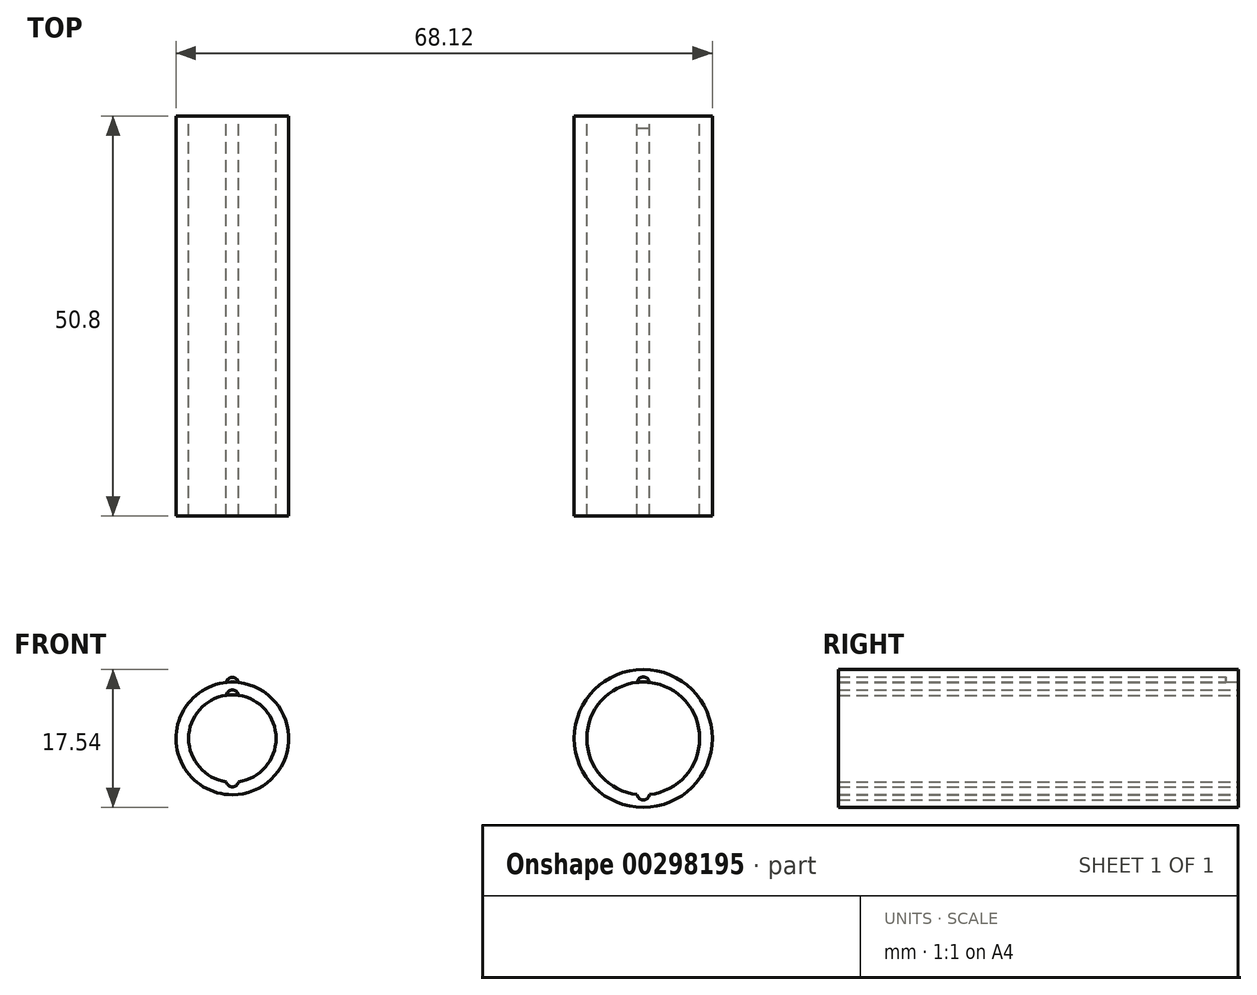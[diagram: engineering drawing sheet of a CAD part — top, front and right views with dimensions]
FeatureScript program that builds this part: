
annotation { "Feature Type Name" : "Feature", "Feature Type Description" : "" }
export const myFeature = defineFeature(function(context is Context, id is Id, definition is map)
    precondition{}
    {
        {
            var Q0;
            Q0=qCreatedBy(makeId("Front.planeOp"),FACE);
            var sketch = newSketch(context, id + "F0", { "sketchPlane" : qUnion([Q0])});
            skCircle(sketch, "E0", {"center": v(-52.2, 0) * mm, "radius": 5.55 * mm});
            skArc(sketch, "E1", {"start": v(-51.41, 5.5) * mm, "mid": v(-52.2, 6.15) * mm, "end": v(-52.98, 5.5) * mm});
            skArc(sketch, "E2.MirrorCS", {"start": v(-51.41, -5.5) * mm, "mid": v(-52.2, -6.15) * mm, "end": v(-52.98, -5.5) * mm});
            skCircle(sketch, "E3", {"center": v(-52.2, 0) * mm, "radius": 7.16 * mm});
            skArc(sketch, "E4", {"start": v(-51.41, 7.11) * mm, "mid": v(-52.2, 7.75) * mm, "end": v(-52.98, 7.11) * mm});
            skArc(sketch, "E5.MirrorCS", {"start": v(-51.41, -7.11) * mm, "mid": v(-52.2, -7.75) * mm, "end": v(-52.98, -7.11) * mm});
            skSolve(sketch);
        }
        {
            var Q0;
            {var subQ0=sQuery(id+"F0.wireOp",EDGE,"989fonS6-DCI9-Xsph-8poP-fN17gT7lNFCT");var subQ3=sQuery(id+"F0.wireOp",EDGE,"9SPTYYTQ-VdL9-9Wax-ncZg-mlvlZ5eD6Vp3");var subQ5=makeQuery(id+"F0.imprint","INTERSECT",VERTEX,{"derivedFrom":[subQ0,subQ3]});Q0=makeQuery(id+"F0.imprint","IMPRINT",FACE,{"disambiguationData":[TD([[makeQuery(id+"F0.imprint","IMPRINT",EDGE,{"disambiguationData":[TD([[subQ5,-1.0]])],"derivedFrom":subQ0}),1.0]])]});}
            var Q1;
            {var subQ1=sQuery(id+"F0.wireOp",EDGE,"989fonS6-DCI9-Xsph-8poP-fN17gT7lNFCT");var subQ4=sQuery(id+"F0.wireOp",EDGE,"9SPTYYTQ-VdL9-9Wax-ncZg-mlvlZ5eD6Vp3");var subQ6=makeQuery(id+"F0.imprint","INTERSECT",VERTEX,{"derivedFrom":[subQ1,subQ4]});Q1=makeQuery(id+"F0.imprint","IMPRINT",FACE,{"disambiguationData":[TD([[makeQuery(id+"F0.imprint","IMPRINT",EDGE,{"disambiguationData":[TD([[subQ6,-1.0]])],"derivedFrom":subQ1}),-1.0]])]});}
            var Q2;
            {var subQ0=sQuery(id+"F0.wireOp",EDGE,"umcB0eHT-4so1-jZ8v-9NKV-PrQTAY5CJR8B");Q2=makeQuery(id+"F0.imprint","IMPRINT",FACE,{"disambiguationData":[TD([[makeQuery(id+"F0.imprint","IMPRINT",EDGE,{"derivedFrom":subQ0}),-1.0]])]});}
            var Q3;
            {var subQ0=sQuery(id+"F0.wireOp",EDGE,"f3edb4b3-b429-4efd-8aee-323062dacc900.MirrorCS");var subQ1=sQuery(id+"F0.wireOp",EDGE,"izCre8lw-zIuZ-BvPA-PBmO-Y99l2bE8kLr2");var subQ2=makeQuery(id+"F0.imprint","INTERSECT",VERTEX,{"disambiguationData":[OD(1.0)],"derivedFrom":[subQ1,subQ0]});Q3=makeQuery(id+"F0.imprint","IMPRINT",FACE,{"disambiguationData":[TD([[makeQuery(id+"F0.imprint","IMPRINT",EDGE,{"disambiguationData":[TD([[subQ2,-1.0]])],"derivedFrom":subQ1}),-1.0]])]});}
            var Q4;
            {var subQ0=sQuery(id+"F0.wireOp",EDGE,"f3edb4b3-b429-4efd-8aee-323062dacc900.MirrorCS");var subQ1=sQuery(id+"F0.wireOp",EDGE,"izCre8lw-zIuZ-BvPA-PBmO-Y99l2bE8kLr2");var subQ2=makeQuery(id+"F0.imprint","INTERSECT",VERTEX,{"disambiguationData":[OD(0.0)],"derivedFrom":[subQ1,subQ0]});Q4=makeQuery(id+"F0.imprint","IMPRINT",FACE,{"disambiguationData":[TD([[makeQuery(id+"F0.imprint","IMPRINT",EDGE,{"disambiguationData":[TD([[subQ2,1.0]])],"derivedFrom":subQ1}),-1.0]])]});}
            var Q5;
            {var subQ0=sQuery(id+"F0.wireOp",EDGE,"989fonS6-DCI9-Xsph-8poP-fN17gT7lNFCT");var subQ5=sQuery(id+"F0.wireOp",EDGE,"E1");var subQ6=makeQuery(id+"F0.imprint","INTERSECT",VERTEX,{"derivedFrom":[subQ0,subQ5]});Q5=makeQuery(id+"F0.imprint","IMPRINT",FACE,{"disambiguationData":[TD([[makeQuery(id+"F0.imprint","IMPRINT",EDGE,{"disambiguationData":[TD([[subQ6,1.0]])],"derivedFrom":subQ0}),1.0]])]});}
            var Q6;
            {var subQ0=sQuery(id+"F0.wireOp",EDGE,"umcB0eHT-4so1-jZ8v-9NKV-PrQTAY5CJR8B");Q6=makeQuery(id+"F0.imprint","IMPRINT",FACE,{"disambiguationData":[TD([[makeQuery(id+"F0.imprint","IMPRINT",EDGE,{"derivedFrom":subQ0}),1.0]])]});}
            var Q7;
            {var subQ1=sQuery(id+"F0.wireOp",EDGE,"izCre8lw-zIuZ-BvPA-PBmO-Y99l2bE8kLr2");var subQ9=makeQuery(id+"F0.imprint","INTERSECT",VERTEX,{"disambiguationData":[OD(1.0)],"derivedFrom":[subQ1,sQuery(id+"F0.wireOp",EDGE,"f3edb4b3-b429-4efd-8aee-323062dacc900.MirrorCS")]});Q7=makeQuery(id+"F0.imprint","IMPRINT",FACE,{"disambiguationData":[TD([[makeQuery(id+"F0.imprint","IMPRINT",EDGE,{"disambiguationData":[TD([[subQ9,-1.0]])],"derivedFrom":subQ1}),1.0]])]});}
            var Q8;
            {var subQ1=sQuery(id+"F0.wireOp",EDGE,"izCre8lw-zIuZ-BvPA-PBmO-Y99l2bE8kLr2");var subQ10=makeQuery(id+"F0.imprint","INTERSECT",VERTEX,{"disambiguationData":[OD(0.0)],"derivedFrom":[subQ1,sQuery(id+"F0.wireOp",EDGE,"f3edb4b3-b429-4efd-8aee-323062dacc900.MirrorCS")]});Q8=makeQuery(id+"F0.imprint","IMPRINT",FACE,{"disambiguationData":[TD([[makeQuery(id+"F0.imprint","IMPRINT",EDGE,{"disambiguationData":[TD([[subQ10,1.0]])],"derivedFrom":subQ1}),1.0]])]});}
            var Q9;
            {var subQ1=sQuery(id+"F0.wireOp",EDGE,"E1");Q9=makeQuery(id+"F0.imprint","IMPRINT",FACE,{"disambiguationData":[TD([[makeQuery(id+"F0.imprint","IMPRINT",EDGE,{"derivedFrom":subQ1}),-1.0]])]});}
            extrude(context, id + "F1", {"entities" : qUnion([Q0, Q1, Q2, Q3, Q4, Q5, Q6, Q7, Q8, Q9]), "depth" : 50.8 * mm});
        }
        {
            var Q0;
            {var subQ0=sQuery(id+"F0.wireOp",EDGE,"E4");var subQ1=sQuery(id+"F0.wireOp",EDGE,"989fonS6-DCI9-Xsph-8poP-fN17gT7lNFCT");var subQ2=makeQuery(id+"F0.imprint","INTERSECT",VERTEX,{"derivedFrom":[subQ1,subQ0]});Q0=makeQuery(id+"F0.imprint","IMPRINT",FACE,{"disambiguationData":[TD([[makeQuery(id+"F0.imprint","IMPRINT",EDGE,{"disambiguationData":[TD([[subQ2,-1.0]])],"derivedFrom":subQ1}),-1.0]])]});}
            var Q1;
            {var subQ0=sQuery(id+"F0.wireOp",EDGE,"E4");var subQ1=sQuery(id+"F0.wireOp",EDGE,"989fonS6-DCI9-Xsph-8poP-fN17gT7lNFCT");var subQ2=makeQuery(id+"F0.imprint","INTERSECT",VERTEX,{"derivedFrom":[subQ1,subQ0]});Q1=makeQuery(id+"F0.imprint","IMPRINT",FACE,{"disambiguationData":[TD([[makeQuery(id+"F0.imprint","IMPRINT",EDGE,{"disambiguationData":[TD([[subQ2,-1.0]])],"derivedFrom":subQ1}),1.0]])]});}
            var Q2;
            {var subQ0=sQuery(id+"F0.wireOp",EDGE,"E1");var subQ1=sQuery(id+"F0.wireOp",EDGE,"E0");var subQ2=makeQuery(id+"F0.imprint","INTERSECT",VERTEX,{"disambiguationData":[OD(1.0)],"derivedFrom":[subQ1,subQ0]});Q2=makeQuery(id+"F0.imprint","IMPRINT",FACE,{"disambiguationData":[TD([[makeQuery(id+"F0.imprint","IMPRINT",EDGE,{"disambiguationData":[TD([[subQ2,1.0]])],"derivedFrom":subQ1}),-1.0]])]});}
            var Q3;
            {var subQ0=sQuery(id+"F0.wireOp",EDGE,"E1");var subQ1=sQuery(id+"F0.wireOp",EDGE,"E0");var subQ2=makeQuery(id+"F0.imprint","INTERSECT",VERTEX,{"disambiguationData":[OD(0.0)],"derivedFrom":[subQ1,subQ0]});Q3=makeQuery(id+"F0.imprint","IMPRINT",FACE,{"disambiguationData":[TD([[makeQuery(id+"F0.imprint","IMPRINT",EDGE,{"disambiguationData":[TD([[subQ2,-1.0]])],"derivedFrom":subQ1}),-1.0]])]});}
            var Q4;
            {var subQ0=sQuery(id+"F0.wireOp",EDGE,"E2.MirrorCS");var subQ1=sQuery(id+"F0.wireOp",EDGE,"E0");var subQ2=makeQuery(id+"F0.imprint","INTERSECT",VERTEX,{"disambiguationData":[OD(1.0)],"derivedFrom":[subQ1,subQ0]});Q4=makeQuery(id+"F0.imprint","IMPRINT",FACE,{"disambiguationData":[TD([[makeQuery(id+"F0.imprint","IMPRINT",EDGE,{"disambiguationData":[TD([[subQ2,-1.0]])],"derivedFrom":subQ1}),-1.0]])]});}
            var Q5;
            {var subQ0=sQuery(id+"F0.wireOp",EDGE,"E2.MirrorCS");var subQ1=sQuery(id+"F0.wireOp",EDGE,"E0");var subQ2=makeQuery(id+"F0.imprint","INTERSECT",VERTEX,{"disambiguationData":[OD(0.0)],"derivedFrom":[subQ1,subQ0]});Q5=makeQuery(id+"F0.imprint","IMPRINT",FACE,{"disambiguationData":[TD([[makeQuery(id+"F0.imprint","IMPRINT",EDGE,{"disambiguationData":[TD([[subQ2,1.0]])],"derivedFrom":subQ1}),-1.0]])]});}
            var Q6;
            {var subQ0=sQuery(id+"F0.wireOp",EDGE,"E5.MirrorCS");var subQ1=sQuery(id+"F0.wireOp",EDGE,"989fonS6-DCI9-Xsph-8poP-fN17gT7lNFCT");var subQ2=makeQuery(id+"F0.imprint","INTERSECT",VERTEX,{"derivedFrom":[subQ1,subQ0]});Q6=makeQuery(id+"F0.imprint","IMPRINT",FACE,{"disambiguationData":[TD([[makeQuery(id+"F0.imprint","IMPRINT",EDGE,{"disambiguationData":[TD([[subQ2,1.0]])],"derivedFrom":subQ1}),1.0]])]});}
            var Q7;
            {var subQ0=sQuery(id+"F0.wireOp",EDGE,"E5.MirrorCS");var subQ1=sQuery(id+"F0.wireOp",EDGE,"989fonS6-DCI9-Xsph-8poP-fN17gT7lNFCT");var subQ2=makeQuery(id+"F0.imprint","INTERSECT",VERTEX,{"derivedFrom":[subQ1,subQ0]});Q7=makeQuery(id+"F0.imprint","IMPRINT",FACE,{"disambiguationData":[TD([[makeQuery(id+"F0.imprint","IMPRINT",EDGE,{"disambiguationData":[TD([[subQ2,1.0]])],"derivedFrom":subQ1}),-1.0]])]});}
            var Q8;
            {var subQ0=sQuery(id+"F0.wireOp",EDGE,"E4");Q8=makeQuery(id+"F0.imprint","IMPRINT",FACE,{"disambiguationData":[TD([[makeQuery(id+"F0.imprint","IMPRINT",EDGE,{"derivedFrom":subQ0}),1.0]])]});}
            var Q9;
            {var subQ0=sQuery(id+"F0.wireOp",EDGE,"E5.MirrorCS");Q9=makeQuery(id+"F0.imprint","IMPRINT",FACE,{"disambiguationData":[TD([[makeQuery(id+"F0.imprint","IMPRINT",EDGE,{"derivedFrom":subQ0}),-1.0]])]});}
            extrude(context, id + "F2", {"entities" : qUnion([Q0, Q1, Q2, Q3, Q4, Q5, Q6, Q7, Q8, Q9]), "operationType" : NewBodyOperationType.ADD, "depth" : 2 / 406.4 * mm});
        }
        {
            var Q0;
            Q0=qCreatedBy(makeId("Front.planeOp"),FACE);
            var sketch = newSketch(context, id + "F3", { "sketchPlane" : qUnion([Q0])});
            skCircle(sketch, "E6", {"center": v(0, 0) * mm, "radius": 7.17 * mm});
            skCircle(sketch, "E7", {"center": v(0, 0) * mm, "radius": 8.77 * mm});
            skArc(sketch, "E8", {"start": v(0.8, 7.12) * mm, "mid": v(0, 7.8) * mm, "end": v(-0.78, 7.13) * mm});
            skArc(sketch, "E9.MirrorCS", {"start": v(0.8, -7.12) * mm, "mid": v(0, -7.8) * mm, "end": v(-0.78, -7.13) * mm});
            skSolve(sketch);
        }
        {
            var Q0;
            Q0=makeQuery(id+"F3.imprint","IMPRINT",FACE,{"disambiguationData":[TD([[makeQuery(id+"F3.imprint","IMPRINT",EDGE,{"derivedFrom":sQuery(id+"F3.wireOp",EDGE,"E7")}),1.0]])]});
            extrude(context, id + "F4", {"entities" : qUnion([Q0]), "depth" : 50.8 * mm});
        }
        {
            var Q0;
            {var subQ0=sQuery(id+"F3.wireOp",EDGE,"E8");Q0=makeQuery(id+"F3.imprint","IMPRINT",FACE,{"disambiguationData":[TD([[makeQuery(id+"F3.imprint","IMPRINT",EDGE,{"derivedFrom":subQ0}),1.0]])]});}
            var Q1;
            {var subQ0=sQuery(id+"F3.wireOp",EDGE,"E9.MirrorCS");Q1=makeQuery(id+"F3.imprint","IMPRINT",FACE,{"disambiguationData":[TD([[makeQuery(id+"F3.imprint","IMPRINT",EDGE,{"derivedFrom":subQ0}),-1.0]])]});}
            extrude(context, id + "F5", {"entities" : qUnion([Q0, Q1]), "operationType" : NewBodyOperationType.ADD, "depth" : 1.57 * mm});
        }
    });
